# Revit family: Playground-System_Ultimate_Fixed-Height_BA873-74
name_source: partatom
category: Generic Models
revit_build: Autodesk Revit 2018 (Build: 20180423_1000(x64)
units: mm (PartAtom-declared; Revit-internal decimal feet)

## family parameters
Always vertical = Yes
Can host rebar = No
Cut with Voids When Loaded = No
OmniClass Number = 23.40.50.34.14
OmniClass Title = Gymnasium Equipment
Part Type = Normal
Room Calculation Point = No
Round Connector Dimension = Use Diameter
Shared = No
Work Plane-Based = No

## types (3) — shared parameters
Backboard Height = 3' - 6"
Backboard Length = 6' - 0"
Basket Netting = Finish - IPI by Bison - White Netting
Building Codes = https://www.brpbybison.com
Construction Details = https://www.arcat.com
Description = IPI by Bison Gymnasium Equipment
Embedding Depth = 4' - 0"
Green Building-LEED = https://www.arcat.com
Hoop Elevation = 10' - 0"
Hoop Finish = Powder Coat - Playground Orange
Installation-Fabrication = http://www.ipibybison.com
Keynote = 11 66 00
Manufacturer = BRP by bison
Manufacturer Fax = 888-438-5312
Manufacturer Website = http://www.ipibybison.com
Model = As Specified
Padding = Padding - Black
Post Height = 8' - 4"
Post Material = Steel - Galvanized - Hot Dipped
Post Square Width = 0' - 6"
Product Data = http://www.arcat.com
Revision = R1_2018-09
Sales Information = http://www.ipibybison.com
Specification = https://www.arcat.com
Test Data = http://www.ipibybison.com
URL = https://ipibybison.com

## per-type parameters (varying)
| type | Backboard BA42RG | Backboard BA472PC | Backboard Finish | Basket Type |
| BA874-BK | No | Yes | Steel - Galvanized - Perforated | BA39U |
| BA873U-BK | Yes | No | Powder Coat - White | BA32 |
| BK873-BK | Yes | No | Powder Coat - White | BA32 |

## geometry (parser evidence)
native form markers: Blend x2, Sweep x4
no freeform markers — native parametric forms only
